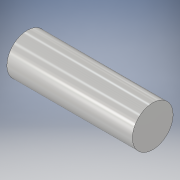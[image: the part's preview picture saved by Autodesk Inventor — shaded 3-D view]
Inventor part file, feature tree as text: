
AUTODESK INVENTOR PART (.ipt)
format: ipt  version: 2019 (Build 230136000, 136)  size: 100,864 bytes
history: native  units: mm
features: extrude x1, sketch x1
ambient origin geometry x8: Origin, YZ Plane, XZ Plane, XY Plane, X Axis, Y Axis, Z Axis, Center Point
bodies: Solid1 (feature_tree)
feature tree (2):
  extrude  "Extrusion1"  Depth=3700.0mm TaperAngle=0.0deg
  sketch  "Sketch1"  dims[d0=1200.0mm d1=3700.0mm d2=0.0mm]
